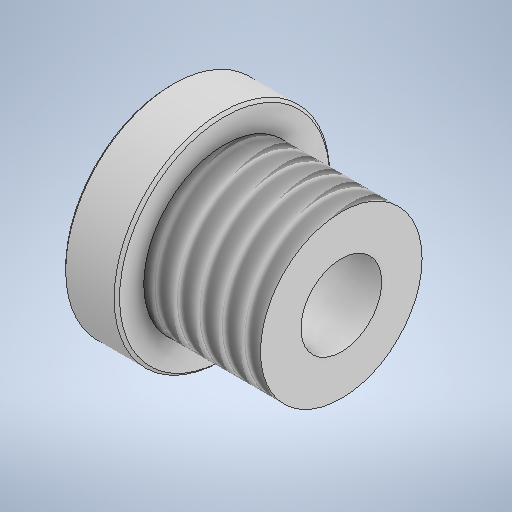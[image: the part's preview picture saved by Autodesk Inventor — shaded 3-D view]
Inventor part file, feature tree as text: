
AUTODESK INVENTOR PART (.ipt)
format: ipt  version: 2025.1 (Build 291241000, 241)  size: 301,056 bytes
history: native  units: mm
features: sketch x2, revolve x1, hole x1, thread x1, plane x1, chamfer x1
ambient origin geometry x8: Origin, YZ Plane, XZ Plane, XY Plane, X Axis, Y Axis, Z Axis, Center Point
bodies: Volumenkörper1 (feature_tree)
feature tree (7):
  revolve  "Umdrehung1"
  hole  "Bohrung1"  [1 undecoded]
  thread  "Gewinde1"  [1 undecoded]
  plane  "Arbeitsebene1"
  chamfer  "Fasen1"  Angle=90.0deg  [1 undecoded]
  sketch  "Skizze1"  dims[d0=24.0mm d1=18.0mm d2=6.0mm]
  sketch  "Skizze2"  dims[d3=13.0mm d4=90.0deg d5=9.0mm d6=6.0mm d7=4.0mm d8=2.0mm d9=90.0deg d10=25.0mm d11=0.0mm d12=18.0mm d13=0.0mm d14=12.0mm d26=0.3mm d27=2.0mm d28=45.0deg]
note: 3 required parameter values undecoded (feature->parameter linkage not recoverable at this tier; creation-order binding heuristic only, values carry confidence <= 0.55)
